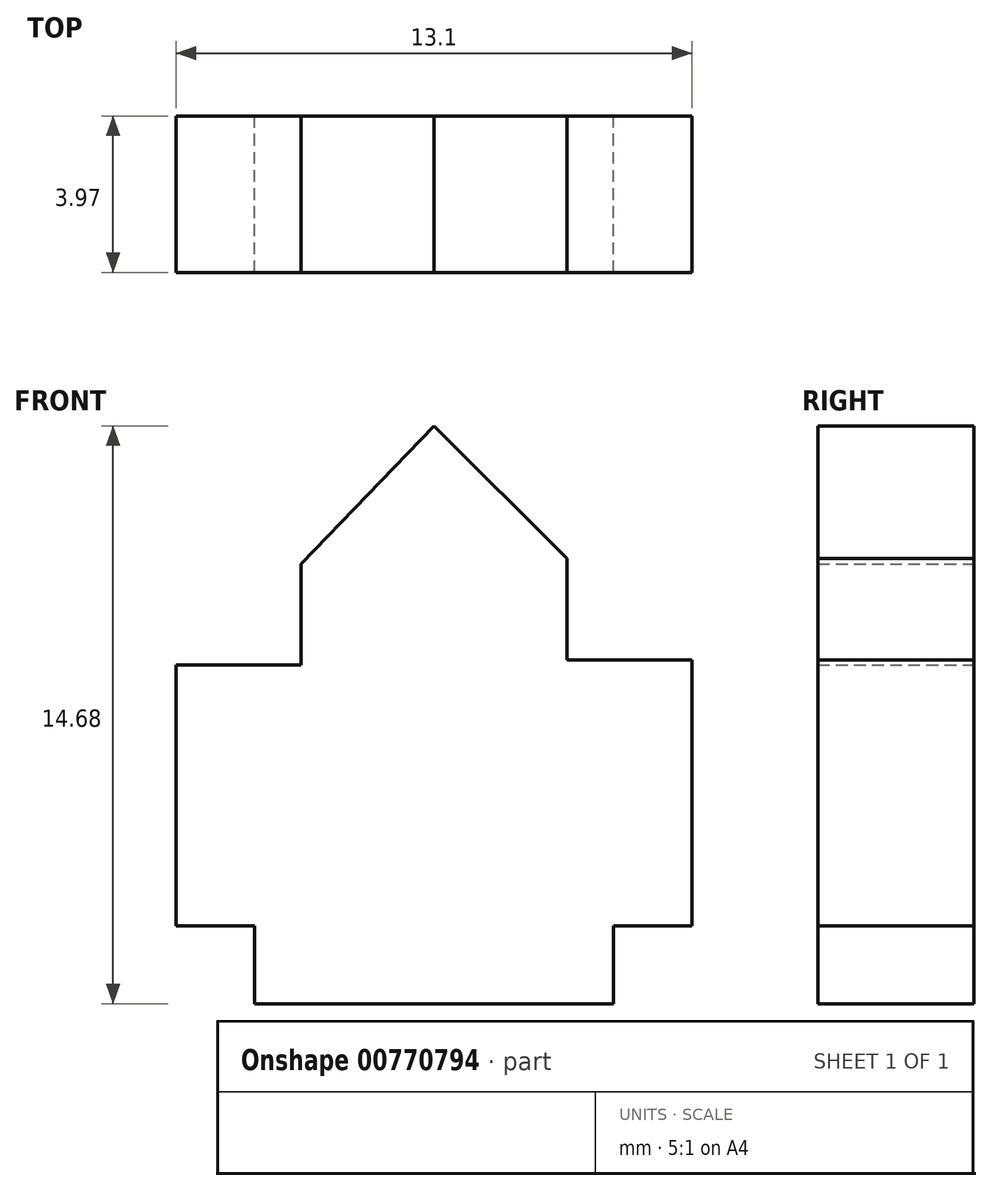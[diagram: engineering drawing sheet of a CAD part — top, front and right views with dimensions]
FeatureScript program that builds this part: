
annotation { "Feature Type Name" : "Feature", "Feature Type Description" : "" }
export const myFeature = defineFeature(function(context is Context, id is Id, definition is map)
    precondition{}
    {
        {
            var Q0;
            Q0=qCreatedBy(makeId("Front.planeOp"),FACE);
            var sketch = newSketch(context, id + "F0", { "sketchPlane" : qUnion([Q0])});
            skLineSegment(sketch, "E0", {"start": v(0, 9) * mm, "end": v(0, -5.67) * mm});
            skLineSegment(sketch, "E1", {"start": v(0, -5.67) * mm, "end": v(4.56, -5.67) * mm});
            skLineSegment(sketch, "E2", {"start": v(0, -5.67) * mm, "end": v(-4.56, -5.67) * mm});
            skLineSegment(sketch, "E3", {"start": v(-4.56, -5.67) * mm, "end": v(-4.56, -3.7) * mm});
            skLineSegment(sketch, "E4", {"start": v(4.56, -5.67) * mm, "end": v(4.56, -3.7) * mm});
            skLineSegment(sketch, "E5", {"start": v(-4.56, -3.7) * mm, "end": v(-6.55, -3.7) * mm});
            skLineSegment(sketch, "E6", {"start": v(4.56, -3.7) * mm, "end": v(6.55, -3.7) * mm});
            skLineSegment(sketch, "E7", {"start": v(-6.55, -3.7) * mm, "end": v(-6.55, 2.94) * mm});
            skLineSegment(sketch, "E8", {"start": v(6.55, -3.7) * mm, "end": v(6.55, 3.06) * mm});
            skLineSegment(sketch, "E9", {"start": v(-6.55, 2.94) * mm, "end": v(-3.37, 2.94) * mm});
            skLineSegment(sketch, "E10", {"start": v(6.55, 3.06) * mm, "end": v(3.37, 3.06) * mm});
            skLineSegment(sketch, "E11", {"start": v(-3.37, 2.94) * mm, "end": v(-3.37, 5.5) * mm});
            skLineSegment(sketch, "E12", {"start": v(3.37, 3.06) * mm, "end": v(3.37, 5.64) * mm});
            skLineSegment(sketch, "E13", {"start": v(-3.37, 5.5) * mm, "end": v(0, 9) * mm});
            skLineSegment(sketch, "E14", {"start": v(0, 9) * mm, "end": v(3.37, 5.64) * mm});
            skSolve(sketch);
        }
        {
            var Q0;
            Q0=qSketchRegion(id+"F0",true);
            extrude(context, id + "F1", {"entities" : qUnion([Q0]), "depth" : 3.97 * mm, "offsetDistance" : 25.4 * mm});
        }
    });
